# Revit family: rmeadvancedsamplefamily
name_source: partatom
category: Mechanical Equipment
units: mm (PartAtom-declared; Revit-internal decimal feet)

## family parameters
Always vertical = Yes
Cut with Voids When Loaded = No
OmniClass Number = 23.75.70.17.27
OmniClass Title = Fan Coil Units
Part Type = Normal
Room Calculation Point = No
Round Connector Dimension = Use Diameter
Shared = No
Work Plane-Based = No

## types (7) — shared parameters
CFU Material = <By Category>
Load Classification = Cooling
Number of Poles = 1
Voltage = 120 V
zero-valued in all types: Default Elevation

## per-type parameters (varying)
| type | Apparent Load | C1 Offset 1 | C2 Offset 1 | Return Air Width | Sensible Cooling Capacity | Supply Air Height | Supply Air Width | Total Cooling Capacity | Unit Height | Unit Length |
| 94 LPS | 50 VA | 108 mm  [stored 0.354331 ft] | 108 mm  [stored 0.354331 ft] | 475 mm | 1348 W | 150 mm | 400 mm | 1758 W | 222 mm | 540 mm |
| 141 LPS | 85 VA | 108 mm  [stored 0.354331 ft] | 108 mm  [stored 0.354331 ft] | 550 mm | 2022 W | 150 mm | 500 mm | 2638 W | 222 mm | 641 mm |
| 188 LPS | 165 VA | 108 mm  [stored 0.354331 ft] | 108 mm  [stored 0.354331 ft] | 700 mm | 3019 W | 150 mm | 650 mm | 3898 W | 222 mm | 794 mm |
| 282 LPS | 225 VA | 92 mm | 124 mm | 850 mm | 4279 W | 200 mm | 800 mm | 5275 W | 254 mm | 921 mm |
| 376 LPS | 235 VA | 92 mm | 124 mm | 1000 mm | 4953 W | 200 mm | 950 mm | 6623 W | 254 mm | 1099 mm |
| 470 LPS | 305 VA | 124 mm | 86 mm | 1400 mm | 6154 W | 200 mm | 1300 mm | 8059 W | 254 mm | 1454 mm |
| 564 LPS | 435 VA | 124 mm | 86 mm | 1600 mm | 7327 W | 200 mm | 1500 mm | 9613 W | 254 mm | 1657 mm |

note: [stored X ft] marks values corroborated as IEEE doubles in the binary element streams (Revit-internal decimal feet)

## geometry (parser evidence)
native form markers: Sweep x2
no freeform markers — native parametric forms only
